# Revit family: ВентКлиматСтрой Вентилятор дымоудаления крышный радиальный ВКРВ
name_source: partatom
category: Оборудование
units: mm (PartAtom-declared; Revit-internal decimal feet)

## family parameters
Всегда вертикально = Да
Заголовок OmniClass = Fans for Air Ductwork
На основе рабочей плоскости = Нет
Номер OmniClass = 23.75.35.17.11
Общий = Нет
При загрузке вырезать с полостями = Нет
Размер круглого соединителя = Использовать диаметр
Тип детали = Нормальный
Точка расчета площади = Да

## types (12) — shared parameters
ADSK_Версия Revit = 2019
ADSK_Версия семейства = rev.1
ADSK_Единица измерения = шт.
ADSK_Классификация нагрузок = Прочее
ADSK_Количество = 1
ADSK_Количество фаз числовое = 3
ADSK_Напряжение = 380 В
ADSK_Предел огнестойкости = 120
ADSK_Предел огнестойкости экземпляра = 120 мин.
Data = ВКРВ
Poles = 3
Описание = Вентилятор дымоудаления крышный радиальный с выходом потока вверх
УГО_3D = Да
zero-valued in all types: ADSK_Материал тип подсчета

## per-type parameters (varying)
| type | .l | A | B | B1 | D | E | E1 | H | H1 | H2 | H3 | STM_A | STM_B | STM_C | d | h | l1 | l2 | МинРазмерШахты |
| ВКРВ-3,55ДУ | 150 мм | 530 мм | 595 мм | 535 мм | 355 мм | 635 мм | 548 мм | 690 мм | 173 мм | 104 мм | 207 мм | 520 мм | 685 мм | 420 мм | 11 мм | 35 мм | 285 мм | 93 мм | 500 мм |
| ВКРВ-4ДУ | 150 мм | 530 мм | 595 мм | 535 мм | 400 мм | 635 мм | 548 мм | 690 мм | 173 мм | 104 мм | 207 мм | 565 мм | 730 мм | 465 мм | 11 мм | 35 мм | 285 мм | 93 мм | 545 мм |
| ВКРВ-4,5ДУ | 150 мм | 535 мм | 665 мм | 605 мм | 450 мм | 810 мм | 711 мм | 780 мм | 195 мм | 117 мм | 234 мм | 615 мм | 780 мм | 515 мм | 11 мм | 40 мм | 328 мм | 138 мм | 595 мм |
| ВКРВ-5ДУ | 150 мм | 535 мм | 665 мм | 605 мм | 500 мм | 810 мм | 710 мм | 790 мм | 198 мм | 119 мм | 237 мм | 665 мм | 830 мм | 565 мм | 11 мм | 40 мм | 328 мм | 138 мм | 645 мм |
| ВКРВ-5,6ДУ | 150 мм | 750 мм | 940 мм | 880 мм | 560 мм | 1100 мм | 973 мм | 1000 мм | 250 мм | 150 мм | 300 мм | 725 мм | 890 мм | 625 мм | 13 мм | 40 мм | 400 мм | 150 мм | 705 мм |
| ВКРВ-6,3ДУ | 150 мм | 750 мм | 940 мм | 880 мм | 630 мм | 1100 мм | 973 мм | 1000 мм | 250 мм | 150 мм | 300 мм | 790 мм | 960 мм | 695 мм | 13 мм | 40 мм | 400 мм | 150 мм | 775 мм |
| ВКРВ-7,1ДУ | 150 мм | 840 мм | 1010 мм | 950 мм | 710 мм | 1200 мм | 1054 мм | 1155 мм | 289 мм | 173 мм | 347 мм | 875 мм | 1040 мм | 775 мм | 13 мм | 40 мм | 425 мм | 175 мм | 855 мм |
| ВКРВ-8ДУ | 150 мм | 1050 мм | 1250 мм | 1190 мм | 800 мм | 1350 мм | 1160 мм | 1500 мм | 375 мм | 225 мм | 450 мм | 1050 мм | 1210 мм | 865 мм | 16 мм | 50 мм | 463 мм | 213 мм | 945 мм |
| ВКРВ-9ДУ | 150 мм | 1050 мм | 1250 мм | 1190 мм | 900 мм | 1500 мм | 1310 мм | 1500 мм | 375 мм | 225 мм | 450 мм | 1090 мм | 1230 мм | 965 мм | 16 мм | 50 мм | 463 мм | 288 мм | 1045 мм |
| ВКРВ-10ДУ | 1 мм | 1350 мм | 1460 мм | 1400 мм | 1000 мм | 1800 мм | 1584 мм | 1700 мм | 425 мм | 255 мм | 510 мм | 1260 мм | 1420 мм | 1065 мм | 18 мм | 50 мм | 1200 мм | 300 мм | 1145 мм |
| ВКРВ-11,2ДУ | 1 мм | 1350 мм | 1460 мм | 1400 мм | 1120 мм | 1800 мм | 1584 мм | 1700 мм | 425 мм | 255 мм | 510 мм | 1390 мм | 1450 мм | 1185 мм | 18 мм | 50 мм | 1200 мм | 300 мм | 1265 мм |
| ВКРВ-12,5ДУ | 1 мм | 1464 мм | 1746 мм | 1686 мм | 1250 мм | 2000 мм | 1768 мм | 1830 мм | 458 мм | 275 мм | 549 мм | 1545 мм | 1700 мм | 1360 мм | 18 мм | 50 мм | 1255 мм | 255 мм | 1395 мм |
